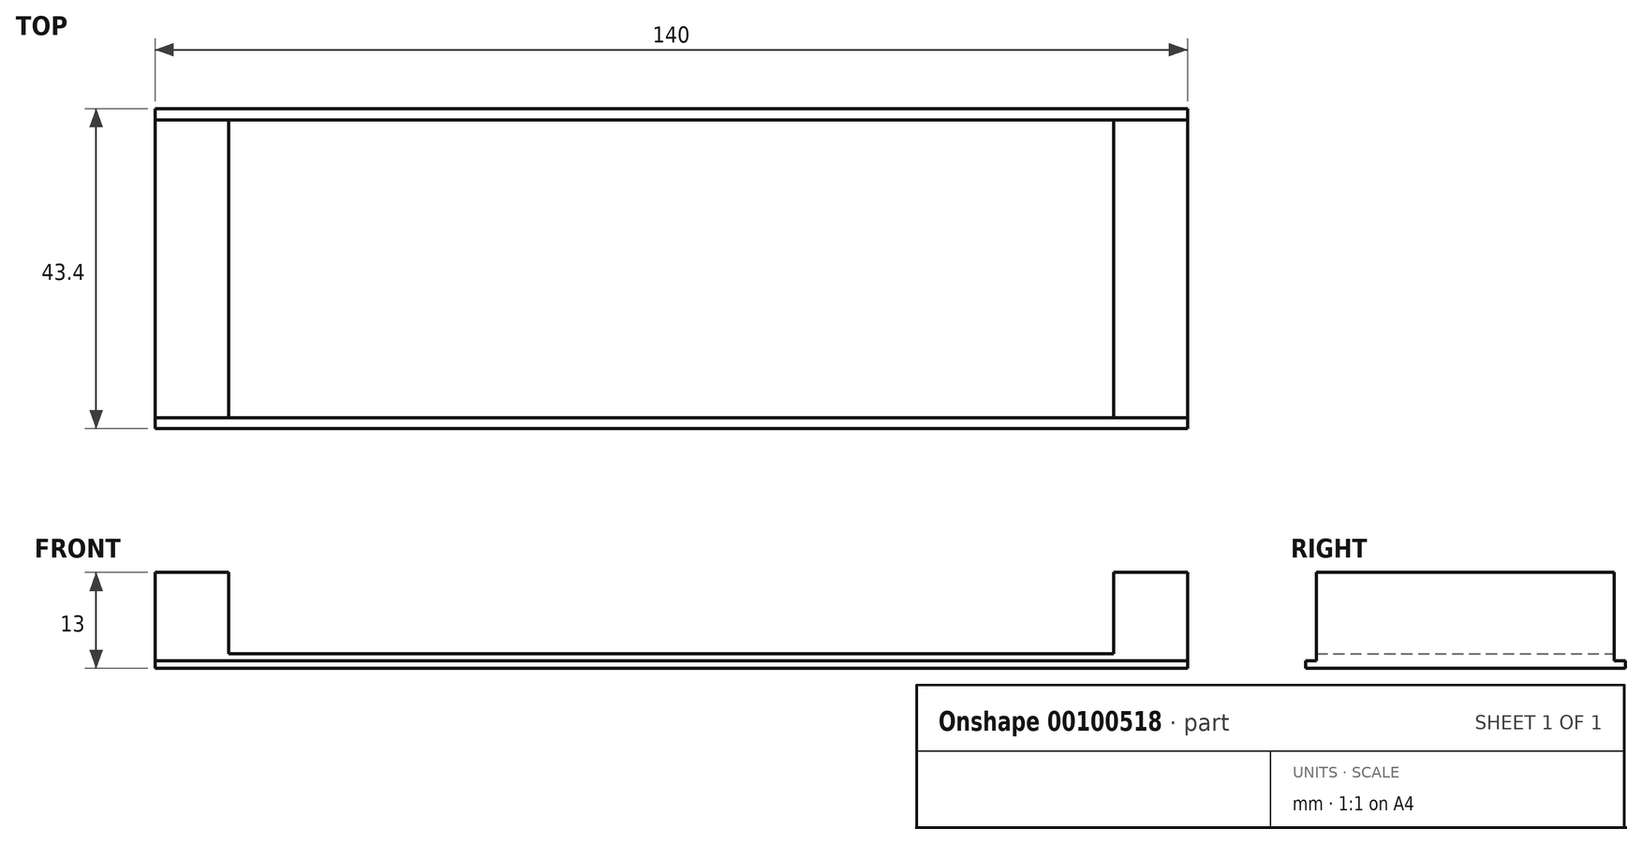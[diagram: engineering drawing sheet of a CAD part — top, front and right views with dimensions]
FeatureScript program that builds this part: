
annotation { "Feature Type Name" : "Feature", "Feature Type Description" : "" }
export const myFeature = defineFeature(function(context is Context, id is Id, definition is map)
    precondition{}
    {
        {
            var Q0;
            Q0=qCreatedBy(makeId("Top.planeOp"),FACE);
            var sketch = newSketch(context, id + "F0", { "sketchPlane" : qUnion([Q0])});
            skLineSegment(sketch, "E0.bottom", {"start": v(70, 20.2) * mm, "end": v(-70, 20.2) * mm});
            skLineSegment(sketch, "E0.top", {"start": v(70, -20.2) * mm, "end": v(-70, -20.2) * mm});
            skLineSegment(sketch, "E0.left", {"start": v(70, 20.2) * mm, "end": v(70, -20.2) * mm});
            skLineSegment(sketch, "E0.right", {"start": v(-70, 20.2) * mm, "end": v(-70, -20.2) * mm});
            skPoint(sketch, "E0.middle", {"position": v(0, 0) * mm});
            skSolve(sketch);
        }
        {
            var Q0;
            Q0 = qSketchRegion(id + "F0", true);
            extrude(context, id + "F1", {"entities" : qUnion([Q0]), "depth" : 1 * mm});
        }
        {
            var Q0;
            Q0=makeQuery(id+"F1.opExtrude","CAP_FACE",FACE,{"disambiguationData":[OSD([sQuery(id+"F0.wireOp",EDGE,"E0.bottom"),sQuery(id+"F0.wireOp",EDGE,"E0.top"),sQuery(id+"F0.wireOp",EDGE,"E0.left"),sQuery(id+"F0.wireOp",EDGE,"E0.right")])],"isStart":false});
            var sketch = newSketch(context, id + "F2", { "sketchPlane" : qUnion([Q0])});
            skLineSegment(sketch, "E1.bottom", {"start": v(-70, -20.2) * mm, "end": v(-60, -20.2) * mm});
            skLineSegment(sketch, "E1.top", {"start": v(-70, 20.2) * mm, "end": v(-60, 20.2) * mm});
            skLineSegment(sketch, "E1.left", {"start": v(-70, -20.2) * mm, "end": v(-70, 20.2) * mm});
            skLineSegment(sketch, "E1.right", {"start": v(-60, -20.2) * mm, "end": v(-60, 20.2) * mm});
            skLineSegment(sketch, "E2.MirrorCS", {"start": v(70, -20.2) * mm, "end": v(60, -20.2) * mm});
            skLineSegment(sketch, "E3.MirrorCS", {"start": v(70, 20.2) * mm, "end": v(60, 20.2) * mm});
            skLineSegment(sketch, "E4.MirrorCS", {"start": v(60, -20.2) * mm, "end": v(60, 20.2) * mm});
            skLineSegment(sketch, "E5.MirrorCS", {"start": v(70, -20.2) * mm, "end": v(70, 20.2) * mm});
            skSolve(sketch);
        }
        {
            var Q0;
            Q0 = qSketchRegion(id + "F2", true);
            extrude(context, id + "F3", {"entities" : qUnion([Q0]), "operationType" : NewBodyOperationType.ADD, "depth" : 11 * mm});
        }
        {
            var Q0;
            Q0=makeQuery(id+"F1.opExtrude","CAP_FACE",FACE,{"disambiguationData":[OSD([sQuery(id+"F0.wireOp",EDGE,"E0.bottom"),sQuery(id+"F0.wireOp",EDGE,"E0.top"),sQuery(id+"F0.wireOp",EDGE,"E0.left"),sQuery(id+"F0.wireOp",EDGE,"E0.right")])],"isStart":true});
            var sketch = newSketch(context, id + "F4", { "sketchPlane" : qUnion([Q0])});
            skLineSegment(sketch, "E6.bottom", {"start": v(-70, 21.7) * mm, "end": v(70, 21.7) * mm});
            skLineSegment(sketch, "E6.top", {"start": v(-70, -21.7) * mm, "end": v(70, -21.7) * mm});
            skLineSegment(sketch, "E6.left", {"start": v(-70, 21.7) * mm, "end": v(-70, -21.7) * mm});
            skLineSegment(sketch, "E6.right", {"start": v(70, 21.7) * mm, "end": v(70, -21.7) * mm});
            skPoint(sketch, "E6.middle", {"position": v(0, 0) * mm});
            skSolve(sketch);
        }
        {
            var Q0;
            Q0 = qSketchRegion(id + "F4", true);
            extrude(context, id + "F5", {"entities" : qUnion([Q0]), "operationType" : NewBodyOperationType.ADD, "depth" : 1 * mm});
        }
    });
